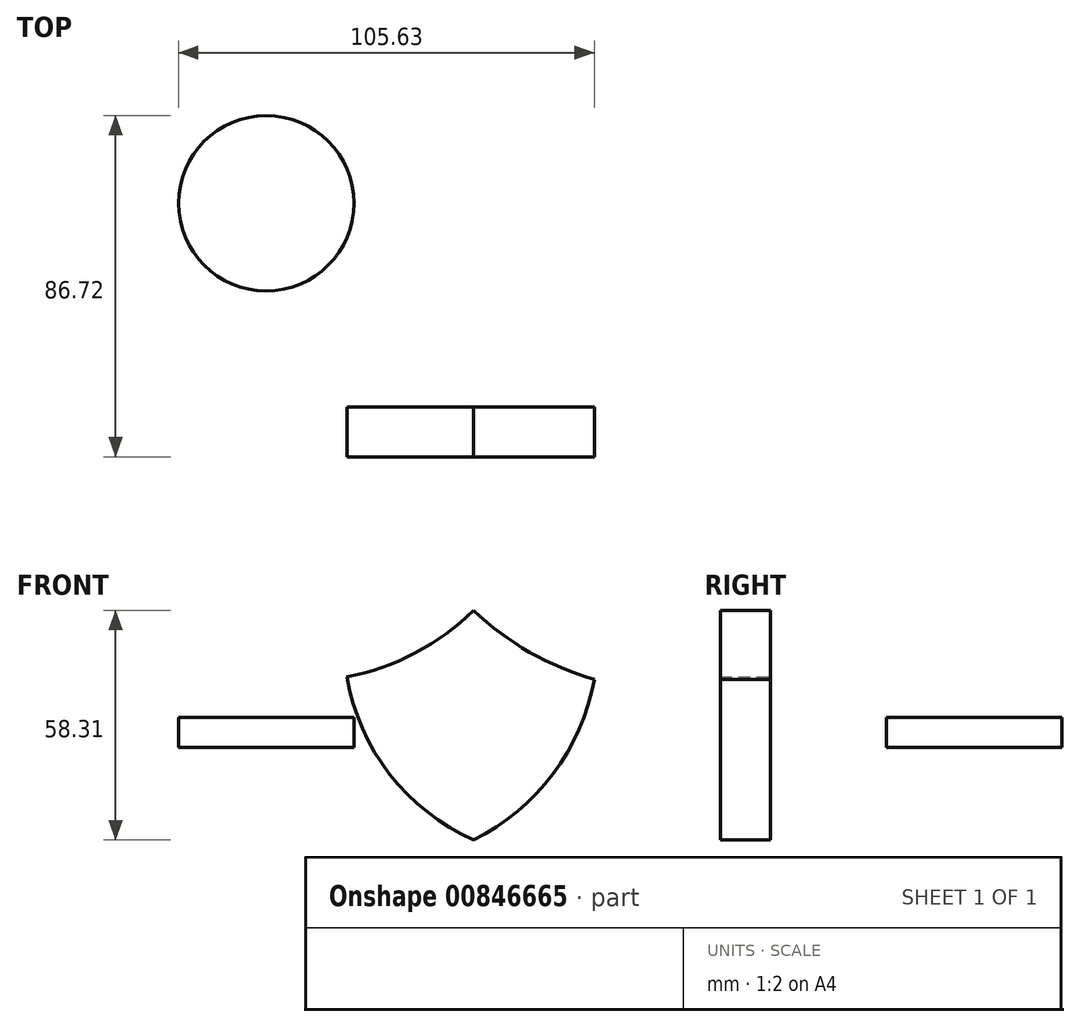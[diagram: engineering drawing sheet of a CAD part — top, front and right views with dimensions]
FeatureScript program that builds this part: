
annotation { "Feature Type Name" : "Feature", "Feature Type Description" : "" }
export const myFeature = defineFeature(function(context is Context, id is Id, definition is map)
    precondition{}
    {
        {
            var Q0;
            Q0=qCreatedBy(makeId("Front.planeOp"),FACE);
            var sketch = newSketch(context, id + "F0", { "sketchPlane" : qUnion([Q0])});
            skArc(sketch, "E0", {"start": v(-32.2, 17.9) * mm, "mid": v(-21.29, -6.86) * mm, "end": v(0, -23.55) * mm});
            skArc(sketch, "E1", {"start": v(0, -23.55) * mm, "mid": v(20.19, -6.79) * mm, "end": v(30.68, 17.27) * mm});
            skArc(sketch, "E2", {"start": v(-32.2, 17.9) * mm, "mid": v(-14.85, 23.93) * mm, "end": v(0, 34.76) * mm});
            skArc(sketch, "E3", {"start": v(0, 34.76) * mm, "mid": v(14.27, 24.14) * mm, "end": v(30.68, 17.27) * mm});
            skSolve(sketch);
        }
        {
            var Q0;
            Q0=makeQuery(id+"F0.imprint","IMPRINT",FACE,{"disambiguationData":[TD([[makeQuery(id+"F0.imprint","IMPRINT",EDGE,{"derivedFrom":sQuery(id+"F0.wireOp",EDGE,"E0")}),1.0]])]});
            extrude(context, id + "F1", {"entities" : qUnion([Q0]), "depth" : 12.7 * mm, "offsetDistance" : 25.4 * mm});
        }
        {
            var Q0;
            Q0=qCreatedBy(makeId("Top.planeOp"),FACE);
            var sketch = newSketch(context, id + "F2", { "sketchPlane" : qUnion([Q0])});
            skCircle(sketch, "E4", {"center": v(-52.67, 51.74) * mm, "radius": 22.28 * mm});
            skSolve(sketch);
        }
        {
            var Q0;
            Q0 = qSketchRegion(id + "F2", true);
            extrude(context, id + "F3", {"entities" : qUnion([Q0]), "depth" : 7.62 * mm, "offsetDistance" : 25.4 * mm});
        }
    });
